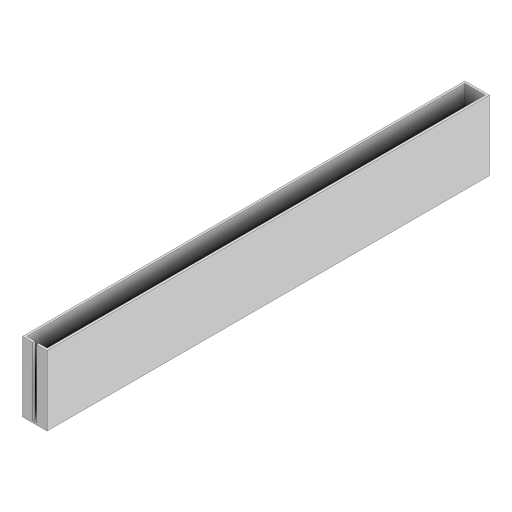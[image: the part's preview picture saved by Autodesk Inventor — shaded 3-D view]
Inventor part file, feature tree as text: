
AUTODESK INVENTOR PART (.ipt)
format: ipt  version: 2024.2 (Build 282272000, 272)  size: 116,224 bytes
history: native  units: in
note: dims shown in document units (in); Inventor stores cm internally (conversion verified against a paired STEP export)
features: extrude x2, sketch x2, shell x1
ambient origin geometry x8: Origin, YZ Plane, XZ Plane, XY Plane, X Axis, Y Axis, Z Axis, Center Point
bodies: Solid1 (feature_tree)
feature tree (5):
  extrude  "Extrusion1"  Depth=12.7075in
  shell  "Shell1"  Thickness=2.0in
  extrude  "Extrusion2"  TaperAngle=0.0deg  [1 undecoded]
  sketch  "Sketch1"  dims[d0=0.7075in d1=12.7075in d2=2.0in d3=0.0in]
  sketch  "Sketch2"  dims[d4=0.0625in d5=0.0in d6=0.24in d7=0.24in d8=0.0625in d9=0.0in]
note: 1 required parameter value undecoded (feature->parameter linkage not recoverable at this tier; creation-order binding heuristic only, values carry confidence <= 0.55)
